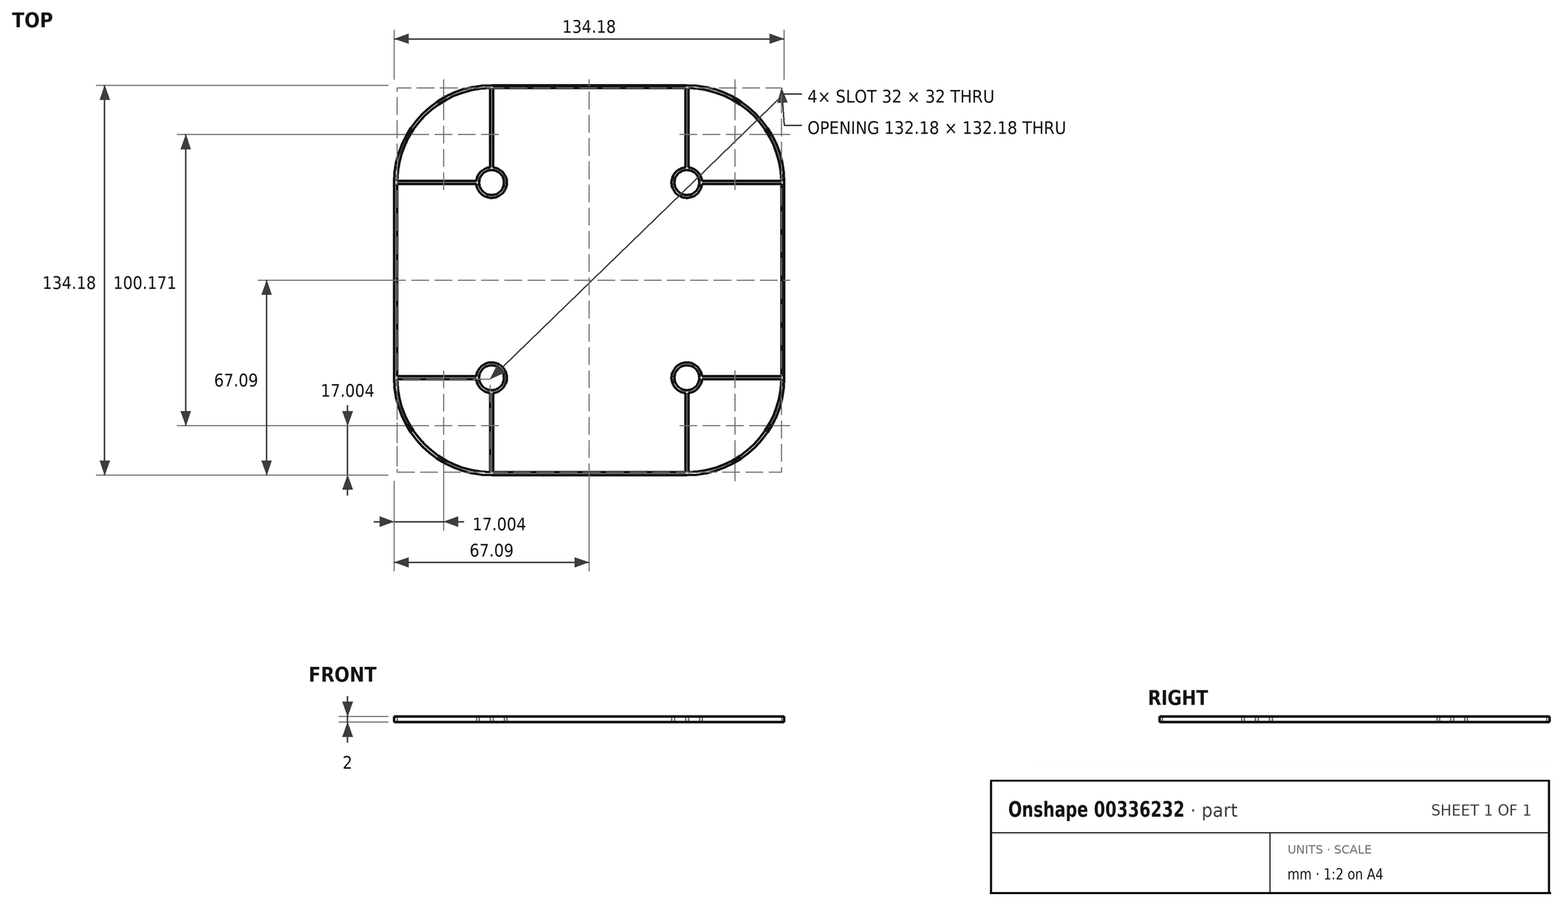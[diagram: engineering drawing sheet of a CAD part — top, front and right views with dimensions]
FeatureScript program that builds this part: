
annotation { "Feature Type Name" : "Feature", "Feature Type Description" : "" }
export const myFeature = defineFeature(function(context is Context, id is Id, definition is map)
    precondition{}
    {
        {
            var Q0;
            Q0=qCreatedBy(makeId("Top.planeOp"),FACE);
            var sketch = newSketch(context, id + "F0", { "sketchPlane" : qUnion([Q0])});
            skLineSegment(sketch, "E0.bottom", {"start": v(33.59, 33.59) * mm, "end": v(-33.59, 33.59) * mm, "construction": true});
            skLineSegment(sketch, "E0.top", {"start": v(33.59, -33.59) * mm, "end": v(-33.59, -33.59) * mm, "construction": true});
            skLineSegment(sketch, "E0.left", {"start": v(33.59, 33.59) * mm, "end": v(33.59, -33.59) * mm, "construction": true});
            skLineSegment(sketch, "E0.right", {"start": v(-33.59, 33.59) * mm, "end": v(-33.59, -33.59) * mm, "construction": true});
            skPoint(sketch, "E0.middle", {"position": v(0, 0) * mm});
            skCircle(sketch, "E1", {"center": v(33.59, 33.59) * mm, "radius": 4.25 * mm, "construction": true});
            skCircle(sketch, "E2", {"center": v(-33.59, 33.59) * mm, "radius": 4.25 * mm, "construction": true});
            skCircle(sketch, "E3", {"center": v(-33.59, -33.59) * mm, "radius": 4.25 * mm, "construction": true});
            skCircle(sketch, "E4", {"center": v(33.59, -33.59) * mm, "radius": 4.25 * mm, "construction": true});
            skLineSegment(sketch, "E5.bottom", {"start": v(10, 16.5) * mm, "end": v(-10, 16.5) * mm, "construction": true});
            skLineSegment(sketch, "E5.top", {"start": v(10, -16.5) * mm, "end": v(-10, -16.5) * mm, "construction": true});
            skLineSegment(sketch, "E5.left", {"start": v(10, 16.5) * mm, "end": v(10, -16.5) * mm, "construction": true});
            skLineSegment(sketch, "E5.right", {"start": v(-10, 16.5) * mm, "end": v(-10, -16.5) * mm, "construction": true});
            skCircle(sketch, "E6", {"center": v(33.59, -33.59) * mm, "radius": 27.5 * mm, "construction": true});
            skCircle(sketch, "E7", {"center": v(-33.59, -33.59) * mm, "radius": 27.5 * mm, "construction": true});
            skCircle(sketch, "E8", {"center": v(-33.59, 33.59) * mm, "radius": 27.5 * mm, "construction": true});
            skCircle(sketch, "E9", {"center": v(33.59, 33.59) * mm, "radius": 27.5 * mm, "construction": true});
            skLineSegment(sketch, "E10", {"start": v(33.59, 33.59) * mm, "end": v(-33.59, -33.59) * mm, "construction": true});
            skSolve(sketch);
        }
        {
            var Q0;
            Q0=qCreatedBy(makeId("Top.planeOp"),FACE);
            var sketch = newSketch(context, id + "F1", { "sketchPlane" : qUnion([Q0])});
            skCircle(sketch, "E11.0", {"center": v(33.59, 33.59) * mm, "radius": 4.25 * mm, "construction": true});
            skCircle(sketch, "E12.0", {"center": v(-33.59, 33.59) * mm, "radius": 4.25 * mm, "construction": true});
            skCircle(sketch, "E13.0", {"center": v(-33.59, -33.59) * mm, "radius": 4.25 * mm, "construction": true});
            skCircle(sketch, "E14.0", {"center": v(33.59, -33.59) * mm, "radius": 4.25 * mm, "construction": true});
            skLineSegment(sketch, "E15.0", {"start": v(33.59, 33.59) * mm, "end": v(33.59, -33.59) * mm, "construction": true});
            skLineSegment(sketch, "E16.0", {"start": v(33.59, 33.59) * mm, "end": v(-33.59, 33.59) * mm, "construction": true});
            skLineSegment(sketch, "E17.0", {"start": v(-33.59, 33.59) * mm, "end": v(-33.59, -33.59) * mm, "construction": true});
            skLineSegment(sketch, "E18.0", {"start": v(33.59, -33.59) * mm, "end": v(-33.59, -33.59) * mm, "construction": true});
            skArc(sketch, "E19.0.startCap", {"start": v(33.59, 39.59) * mm, "mid": v(39.59, 33.59) * mm, "end": v(33.59, 27.59) * mm});
            skArc(sketch, "E19.0.endCap", {"start": v(-33.59, 27.59) * mm, "mid": v(-39.59, 33.59) * mm, "end": v(-33.59, 39.59) * mm});
            skLineSegment(sketch, "E19.0.left", {"start": v(33.59, 27.59) * mm, "end": v(29.5, 27.59) * mm});
            skLineSegment(sketch, "E19.0.right", {"start": v(33.59, 39.59) * mm, "end": v(-33.59, 39.59) * mm});
            skArc(sketch, "E20.0.startCap", {"start": v(33.59, -27.59) * mm, "mid": v(39.59, -33.59) * mm, "end": v(33.59, -39.59) * mm});
            skArc(sketch, "E20.0.endCap", {"start": v(-33.59, -39.59) * mm, "mid": v(-39.59, -33.59) * mm, "end": v(-33.59, -27.59) * mm});
            skLineSegment(sketch, "E20.0.left", {"start": v(33.59, -39.59) * mm, "end": v(-33.59, -39.59) * mm});
            skLineSegment(sketch, "E20.0.right", {"start": v(33.59, -27.59) * mm, "end": v(29.5, -27.59) * mm});
            skLineSegment(sketch, "E21", {"start": v(-17.5, 15.59) * mm, "end": v(-17.5, -15.59) * mm});
            skLineSegment(sketch, "E22", {"start": v(17.5, 15.59) * mm, "end": v(17.5, -15.59) * mm});
            skLineSegment(sketch, "E23.trimOffspring", {"start": v(-29.5, 27.59) * mm, "end": v(-33.59, 27.59) * mm});
            skLineSegment(sketch, "E24.trimOffspring", {"start": v(-29.5, -27.59) * mm, "end": v(-33.59, -27.59) * mm});
            skPoint(sketch, "E25.visualSharp", {"position": v(17.5, 27.59) * mm});
            skArc(sketch, "E25.filletArc", {"start": v(29.5, 27.59) * mm, "mid": v(21.01, 24.07) * mm, "end": v(17.5, 15.59) * mm});
            skPoint(sketch, "E26.visualSharp", {"position": v(-17.5, 27.59) * mm});
            skArc(sketch, "E26.filletArc", {"start": v(-17.5, 15.59) * mm, "mid": v(-21.01, 24.07) * mm, "end": v(-29.5, 27.59) * mm});
            skPoint(sketch, "E27.visualSharp", {"position": v(-17.5, -27.59) * mm});
            skArc(sketch, "E27.filletArc", {"start": v(-29.5, -27.59) * mm, "mid": v(-21.01, -24.07) * mm, "end": v(-17.5, -15.59) * mm});
            skPoint(sketch, "E28.visualSharp", {"position": v(17.5, -27.59) * mm});
            skArc(sketch, "E28.filletArc", {"start": v(17.5, -15.59) * mm, "mid": v(21.01, -24.07) * mm, "end": v(29.5, -27.59) * mm});
            skSolve(sketch);
        }
        {
            var Q0;
            Q0=qCreatedBy(makeId("Top.planeOp"),FACE);
            var sketch = newSketch(context, id + "F2", { "sketchPlane" : qUnion([Q0])});
            skCircle(sketch, "E29.0", {"center": v(33.59, 33.59) * mm, "radius": 4.3 * mm});
            skArc(sketch, "E30.0", {"start": v(33.09, 38.81) * mm, "mid": v(29.88, 29.88) * mm, "end": v(38.81, 33.09) * mm});
            skArc(sketch, "E31.0", {"start": v(33.59, 66.09) * mm, "mid": v(10.6, 10.6) * mm, "end": v(66.09, 33.59) * mm, "construction": true});
            skLineSegment(sketch, "E32", {"start": v(33.59, 33.59) * mm, "end": v(33.59, 66.09) * mm, "construction": true});
            skLineSegment(sketch, "E33", {"start": v(33.59, 33.59) * mm, "end": v(66.09, 33.59) * mm, "construction": true});
            skArc(sketch, "E34", {"start": v(33.59, 66.09) * mm, "mid": v(56.57, 56.57) * mm, "end": v(66.09, 33.59) * mm});
            skArc(sketch, "E35", {"start": v(33.59, 67.09) * mm, "mid": v(57.28, 57.28) * mm, "end": v(67.09, 33.59) * mm});
            skLineSegment(sketch, "E36", {"start": v(33.59, 67.09) * mm, "end": v(0, 67.09) * mm});
            skLineSegment(sketch, "E37", {"start": v(33.09, 66.09) * mm, "end": v(0, 66.09) * mm});
            skLineSegment(sketch, "E38", {"start": v(67.09, 33.59) * mm, "end": v(67.09, 0) * mm});
            skLineSegment(sketch, "E39", {"start": v(66.09, 33.09) * mm, "end": v(66.09, 0) * mm});
            skLineSegment(sketch, "E40", {"start": v(33.09, 66.09) * mm, "end": v(33.09, 38.81) * mm});
            skLineSegment(sketch, "E41", {"start": v(34.09, 66.08) * mm, "end": v(34.09, 38.81) * mm});
            skLineSegment(sketch, "E42", {"start": v(38.81, 33.09) * mm, "end": v(66.09, 33.09) * mm});
            skLineSegment(sketch, "E43", {"start": v(38.81, 34.09) * mm, "end": v(66.08, 34.09) * mm});
            skArc(sketch, "E44.trimOffspring", {"start": v(66.08, 34.09) * mm, "mid": v(56.57, 56.57) * mm, "end": v(34.09, 66.08) * mm, "construction": true});
            skArc(sketch, "E45.trimOffspring", {"start": v(38.81, 34.09) * mm, "mid": v(37.3, 37.3) * mm, "end": v(34.09, 38.81) * mm});
            skLineSegment(sketch, "E46.1.0", {"start": v(-67.09, 33.59) * mm, "end": v(-67.09, 0) * mm});
            skLineSegment(sketch, "E46.1.1", {"start": v(-33.09, 38.81) * mm, "end": v(-33.09, 66.09) * mm});
            skLineSegment(sketch, "E46.1.2", {"start": v(-33.59, 33.59) * mm, "end": v(-66.09, 33.59) * mm, "construction": true});
            skLineSegment(sketch, "E46.1.3", {"start": v(-66.09, 33.09) * mm, "end": v(-66.09, 0) * mm});
            skArc(sketch, "E46.1.4", {"start": v(-66.09, 33.59) * mm, "mid": v(-10.6, 10.6) * mm, "end": v(-33.59, 66.09) * mm, "construction": true});
            skArc(sketch, "E46.1.5", {"start": v(-67.09, 33.59) * mm, "mid": v(-57.28, 57.28) * mm, "end": v(-33.59, 67.09) * mm});
            skLineSegment(sketch, "E46.1.6", {"start": v(-33.09, 66.09) * mm, "end": v(0, 66.09) * mm});
            skArc(sketch, "E46.1.7", {"start": v(-66.09, 33.59) * mm, "mid": v(-56.57, 56.57) * mm, "end": v(-33.59, 66.09) * mm});
            skLineSegment(sketch, "E46.1.8", {"start": v(-66.09, 33.09) * mm, "end": v(-38.81, 33.09) * mm});
            skLineSegment(sketch, "E46.1.9", {"start": v(-33.59, 67.09) * mm, "end": v(0, 67.09) * mm});
            skLineSegment(sketch, "E46.1.10", {"start": v(-33.59, 33.59) * mm, "end": v(-33.59, 66.09) * mm, "construction": true});
            skArc(sketch, "E46.1.11", {"start": v(-34.09, 66.08) * mm, "mid": v(-56.57, 56.57) * mm, "end": v(-66.08, 34.09) * mm, "construction": true});
            skLineSegment(sketch, "E46.1.12", {"start": v(-66.08, 34.09) * mm, "end": v(-38.81, 34.09) * mm});
            skArc(sketch, "E46.1.13", {"start": v(-38.81, 33.09) * mm, "mid": v(-29.88, 29.88) * mm, "end": v(-33.09, 38.81) * mm});
            skLineSegment(sketch, "E46.1.14", {"start": v(-34.09, 38.81) * mm, "end": v(-34.09, 66.08) * mm});
            skCircle(sketch, "E46.1.15", {"center": v(-33.59, 33.59) * mm, "radius": 4.3 * mm});
            skArc(sketch, "E46.1.16", {"start": v(-34.09, 38.81) * mm, "mid": v(-37.3, 37.3) * mm, "end": v(-38.81, 34.09) * mm});
            skLineSegment(sketch, "E46.2.0", {"start": v(-33.59, -67.09) * mm, "end": v(0, -67.09) * mm});
            skLineSegment(sketch, "E46.2.1", {"start": v(-38.81, -33.09) * mm, "end": v(-66.09, -33.09) * mm});
            skLineSegment(sketch, "E46.2.2", {"start": v(-33.59, -33.59) * mm, "end": v(-33.59, -66.09) * mm, "construction": true});
            skLineSegment(sketch, "E46.2.3", {"start": v(-33.09, -66.09) * mm, "end": v(0, -66.09) * mm});
            skArc(sketch, "E46.2.4", {"start": v(-33.59, -66.09) * mm, "mid": v(-10.6, -10.6) * mm, "end": v(-66.09, -33.59) * mm, "construction": true});
            skArc(sketch, "E46.2.5", {"start": v(-33.59, -67.09) * mm, "mid": v(-57.28, -57.28) * mm, "end": v(-67.09, -33.59) * mm});
            skLineSegment(sketch, "E46.2.6", {"start": v(-66.09, -33.09) * mm, "end": v(-66.09, 0) * mm});
            skArc(sketch, "E46.2.7", {"start": v(-33.59, -66.09) * mm, "mid": v(-56.57, -56.57) * mm, "end": v(-66.09, -33.59) * mm});
            skLineSegment(sketch, "E46.2.8", {"start": v(-33.09, -66.09) * mm, "end": v(-33.09, -38.81) * mm});
            skLineSegment(sketch, "E46.2.9", {"start": v(-67.09, -33.59) * mm, "end": v(-67.09, 0) * mm});
            skLineSegment(sketch, "E46.2.10", {"start": v(-33.59, -33.59) * mm, "end": v(-66.09, -33.59) * mm, "construction": true});
            skArc(sketch, "E46.2.11", {"start": v(-66.08, -34.09) * mm, "mid": v(-56.57, -56.57) * mm, "end": v(-34.09, -66.08) * mm, "construction": true});
            skLineSegment(sketch, "E46.2.12", {"start": v(-34.09, -66.08) * mm, "end": v(-34.09, -38.81) * mm});
            skArc(sketch, "E46.2.13", {"start": v(-33.09, -38.81) * mm, "mid": v(-29.88, -29.88) * mm, "end": v(-38.81, -33.09) * mm});
            skLineSegment(sketch, "E46.2.14", {"start": v(-38.81, -34.09) * mm, "end": v(-66.08, -34.09) * mm});
            skCircle(sketch, "E46.2.15", {"center": v(-33.59, -33.59) * mm, "radius": 4.3 * mm});
            skArc(sketch, "E46.2.16", {"start": v(-38.81, -34.09) * mm, "mid": v(-37.3, -37.3) * mm, "end": v(-34.09, -38.81) * mm});
            skLineSegment(sketch, "E46.3.0", {"start": v(67.09, -33.59) * mm, "end": v(67.09, 0) * mm});
            skLineSegment(sketch, "E46.3.1", {"start": v(33.09, -38.81) * mm, "end": v(33.09, -66.09) * mm});
            skLineSegment(sketch, "E46.3.2", {"start": v(33.59, -33.59) * mm, "end": v(66.09, -33.59) * mm, "construction": true});
            skLineSegment(sketch, "E46.3.3", {"start": v(66.09, -33.09) * mm, "end": v(66.09, 0) * mm});
            skArc(sketch, "E46.3.4", {"start": v(66.09, -33.59) * mm, "mid": v(10.6, -10.6) * mm, "end": v(33.59, -66.09) * mm, "construction": true});
            skArc(sketch, "E46.3.5", {"start": v(67.09, -33.59) * mm, "mid": v(57.28, -57.28) * mm, "end": v(33.59, -67.09) * mm});
            skLineSegment(sketch, "E46.3.6", {"start": v(33.09, -66.09) * mm, "end": v(0, -66.09) * mm});
            skArc(sketch, "E46.3.7", {"start": v(66.09, -33.59) * mm, "mid": v(56.57, -56.57) * mm, "end": v(33.59, -66.09) * mm});
            skLineSegment(sketch, "E46.3.8", {"start": v(66.09, -33.09) * mm, "end": v(38.81, -33.09) * mm});
            skLineSegment(sketch, "E46.3.9", {"start": v(33.59, -67.09) * mm, "end": v(0, -67.09) * mm});
            skLineSegment(sketch, "E46.3.10", {"start": v(33.59, -33.59) * mm, "end": v(33.59, -66.09) * mm, "construction": true});
            skArc(sketch, "E46.3.11", {"start": v(34.09, -66.08) * mm, "mid": v(56.57, -56.57) * mm, "end": v(66.08, -34.09) * mm, "construction": true});
            skLineSegment(sketch, "E46.3.12", {"start": v(66.08, -34.09) * mm, "end": v(38.81, -34.09) * mm});
            skArc(sketch, "E46.3.13", {"start": v(38.81, -33.09) * mm, "mid": v(29.88, -29.88) * mm, "end": v(33.09, -38.81) * mm});
            skLineSegment(sketch, "E46.3.14", {"start": v(34.09, -38.81) * mm, "end": v(34.09, -66.08) * mm});
            skCircle(sketch, "E46.3.15", {"center": v(33.59, -33.59) * mm, "radius": 4.3 * mm});
            skArc(sketch, "E46.3.16", {"start": v(34.09, -38.81) * mm, "mid": v(37.3, -37.3) * mm, "end": v(38.81, -34.09) * mm});
            skPoint(sketch, "E46.center", {"position": v(0, 0) * mm});
            skSolve(sketch);
        }
        {
            var Q0;
            Q0 = qSketchRegion(id + "F2", true);
            extrude(context, id + "F3", {"entities" : qUnion([Q0]), "depth" : 2 * mm});
        }
    });
